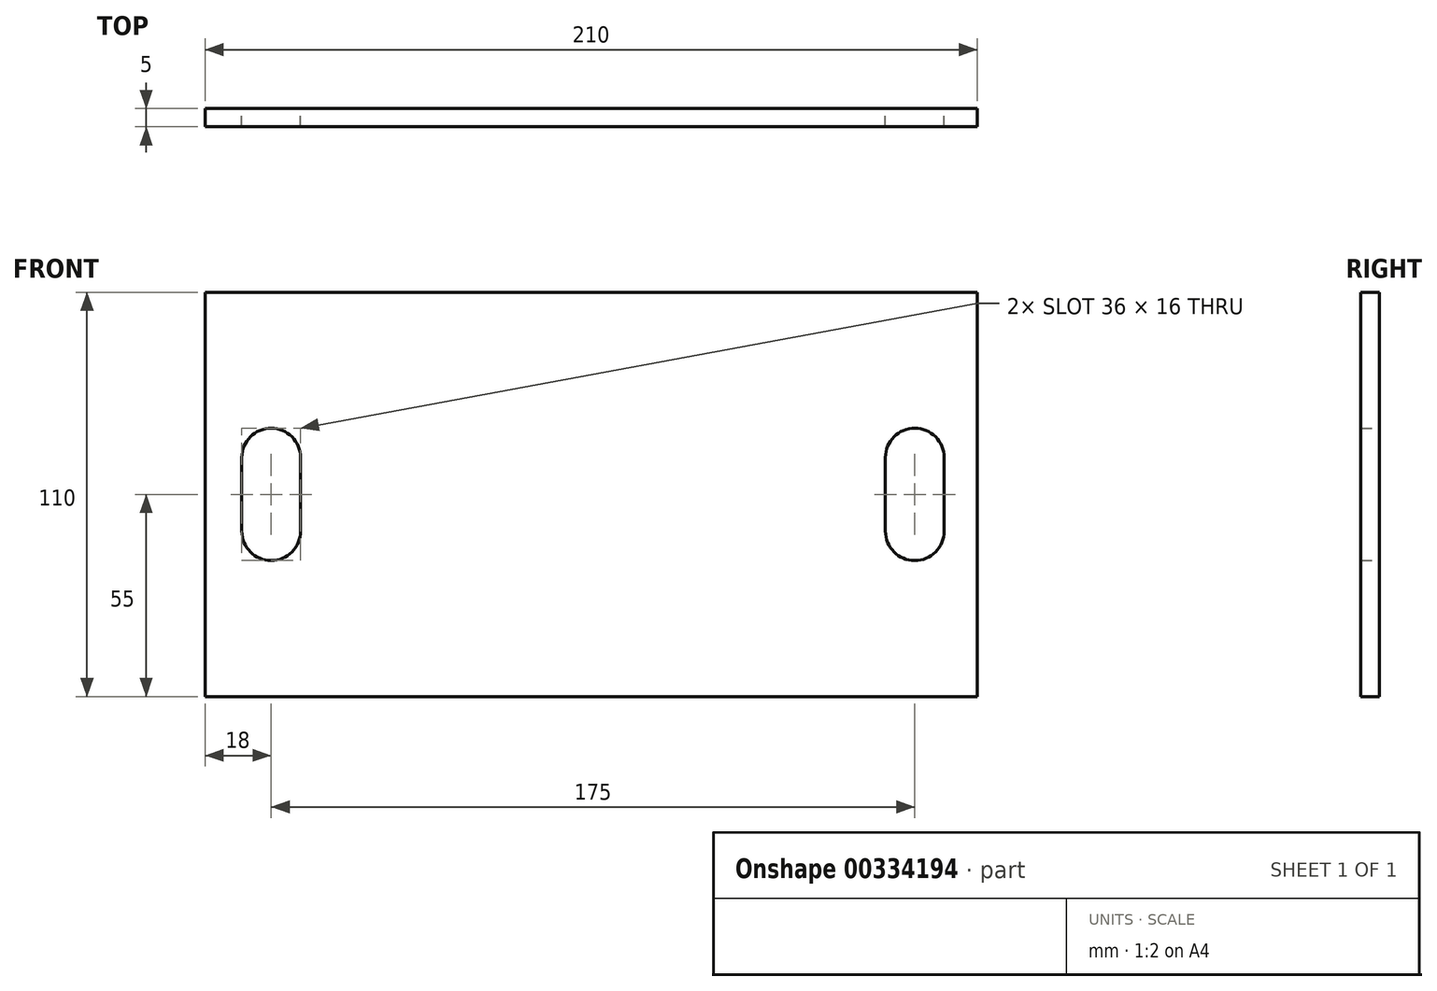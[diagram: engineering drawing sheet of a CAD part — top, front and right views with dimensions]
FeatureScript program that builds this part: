
annotation { "Feature Type Name" : "Feature", "Feature Type Description" : "" }
export const myFeature = defineFeature(function(context is Context, id is Id, definition is map)
    precondition{}
    {
        {
            var Q0;
            Q0=qCreatedBy(makeId("Front.planeOp"),FACE);
            var sketch = newSketch(context, id + "F0", { "sketchPlane" : qUnion([Q0])});
            skLineSegment(sketch, "E0.bottom", {"start": v(105, 55) * mm, "end": v(-105, 55) * mm});
            skLineSegment(sketch, "E0.top", {"start": v(105, -55) * mm, "end": v(-105, -55) * mm});
            skLineSegment(sketch, "E0.left", {"start": v(105, 55) * mm, "end": v(105, -55) * mm});
            skLineSegment(sketch, "E0.right", {"start": v(-105, 55) * mm, "end": v(-105, -55) * mm});
            skPoint(sketch, "E0.middle", {"position": v(0, 0) * mm});
            skLineSegment(sketch, "E1.bottom", {"start": v(-79, -18) * mm, "end": v(-95, -18) * mm});
            skLineSegment(sketch, "E1.top", {"start": v(-79, 18) * mm, "end": v(-95, 18) * mm});
            skLineSegment(sketch, "E1.left", {"start": v(-79, -18) * mm, "end": v(-79, 18) * mm});
            skLineSegment(sketch, "E1.right", {"start": v(-95, -18) * mm, "end": v(-95, 18) * mm});
            skPoint(sketch, "E1.middle", {"position": v(-87, 0) * mm});
            skLineSegment(sketch, "E2.bottom", {"start": v(96, -18) * mm, "end": v(80, -18) * mm});
            skLineSegment(sketch, "E2.top", {"start": v(96, 18) * mm, "end": v(80, 18) * mm});
            skLineSegment(sketch, "E2.left", {"start": v(96, -18) * mm, "end": v(96, 18) * mm});
            skLineSegment(sketch, "E2.right", {"start": v(80, -18) * mm, "end": v(80, 18) * mm});
            skPoint(sketch, "E2.middle", {"position": v(88, 0) * mm});
            skSolve(sketch);
        }
        {
            var Q0;
            Q0=makeQuery(id+"F0.imprint","IMPRINT",FACE,{"disambiguationData":[TD([[makeQuery(id+"F0.imprint","IMPRINT",EDGE,{"derivedFrom":sQuery(id+"F0.wireOp",EDGE,"E0.bottom")}),1.0]])]});
            extrude(context, id + "F1", {"entities" : qUnion([Q0]), "depth" : 5 * mm});
        }
        {
            var Q0;
            Q0=makeQuery(id+"F1.opExtrude","SWEPT_EDGE",EDGE,{"disambiguationData":[OSD([sQuery(id+"F0.wireOp",EDGE,"E1.top"),sQuery(id+"F0.wireOp",EDGE,"E1.right")])]});
            var Q1;
            Q1=makeQuery(id+"F1.opExtrude","SWEPT_EDGE",EDGE,{"disambiguationData":[OSD([sQuery(id+"F0.wireOp",EDGE,"E1.top"),sQuery(id+"F0.wireOp",EDGE,"E1.left")])]});
            var Q2;
            Q2=makeQuery(id+"F1.opExtrude","SWEPT_EDGE",EDGE,{"disambiguationData":[OSD([sQuery(id+"F0.wireOp",EDGE,"E1.bottom"),sQuery(id+"F0.wireOp",EDGE,"E1.right")])]});
            var Q3;
            Q3=makeQuery(id+"F1.opExtrude","SWEPT_EDGE",EDGE,{"disambiguationData":[OSD([sQuery(id+"F0.wireOp",EDGE,"E1.bottom"),sQuery(id+"F0.wireOp",EDGE,"E1.left")])]});
            var Q4;
            Q4=makeQuery(id+"F1.opExtrude","SWEPT_EDGE",EDGE,{"disambiguationData":[OSD([sQuery(id+"F0.wireOp",EDGE,"3c7e9e45-3920-4990-8ff4-15449f359e051.MirrorCS"),sQuery(id+"F0.wireOp",EDGE,"3c7e9e45-3920-4990-8ff4-15449f359e053.MirrorCS")])]});
            var Q5;
            Q5=makeQuery(id+"F1.opExtrude","SWEPT_EDGE",EDGE,{"disambiguationData":[OSD([sQuery(id+"F0.wireOp",EDGE,"3c7e9e45-3920-4990-8ff4-15449f359e050.MirrorCS"),sQuery(id+"F0.wireOp",EDGE,"3c7e9e45-3920-4990-8ff4-15449f359e053.MirrorCS")])]});
            var Q6;
            Q6=makeQuery(id+"F1.opExtrude","SWEPT_EDGE",EDGE,{"disambiguationData":[OSD([sQuery(id+"F0.wireOp",EDGE,"3c7e9e45-3920-4990-8ff4-15449f359e051.MirrorCS"),sQuery(id+"F0.wireOp",EDGE,"3c7e9e45-3920-4990-8ff4-15449f359e052.MirrorCS")])]});
            var Q7;
            Q7=makeQuery(id+"F1.opExtrude","SWEPT_EDGE",EDGE,{"disambiguationData":[OSD([sQuery(id+"F0.wireOp",EDGE,"3c7e9e45-3920-4990-8ff4-15449f359e050.MirrorCS"),sQuery(id+"F0.wireOp",EDGE,"3c7e9e45-3920-4990-8ff4-15449f359e052.MirrorCS")])]});
            var Q8;
            Q8=makeQuery(id+"F1.opExtrude","SWEPT_EDGE",EDGE,{"disambiguationData":[OSD([sQuery(id+"F0.wireOp",EDGE,"E2.top"),sQuery(id+"F0.wireOp",EDGE,"E2.right")])]});
            var Q9;
            Q9=makeQuery(id+"F1.opExtrude","SWEPT_EDGE",EDGE,{"disambiguationData":[OSD([sQuery(id+"F0.wireOp",EDGE,"E2.top"),sQuery(id+"F0.wireOp",EDGE,"E2.left")])]});
            var Q10;
            Q10=makeQuery(id+"F1.opExtrude","SWEPT_EDGE",EDGE,{"disambiguationData":[OSD([sQuery(id+"F0.wireOp",EDGE,"E2.bottom"),sQuery(id+"F0.wireOp",EDGE,"E2.left")])]});
            var Q11;
            Q11=makeQuery(id+"F1.opExtrude","SWEPT_EDGE",EDGE,{"disambiguationData":[OSD([sQuery(id+"F0.wireOp",EDGE,"E2.bottom"),sQuery(id+"F0.wireOp",EDGE,"E2.right")])]});
            fillet(context, id + "F2", {"entities" : qUnion([Q0, Q1, Q2, Q3, Q4, Q5, Q6, Q7, Q8, Q9, Q10, Q11]), "radius" : 8 * mm, "tangentPropagation" : true, "allowEdgeOverflow" : false});
        }
    });
